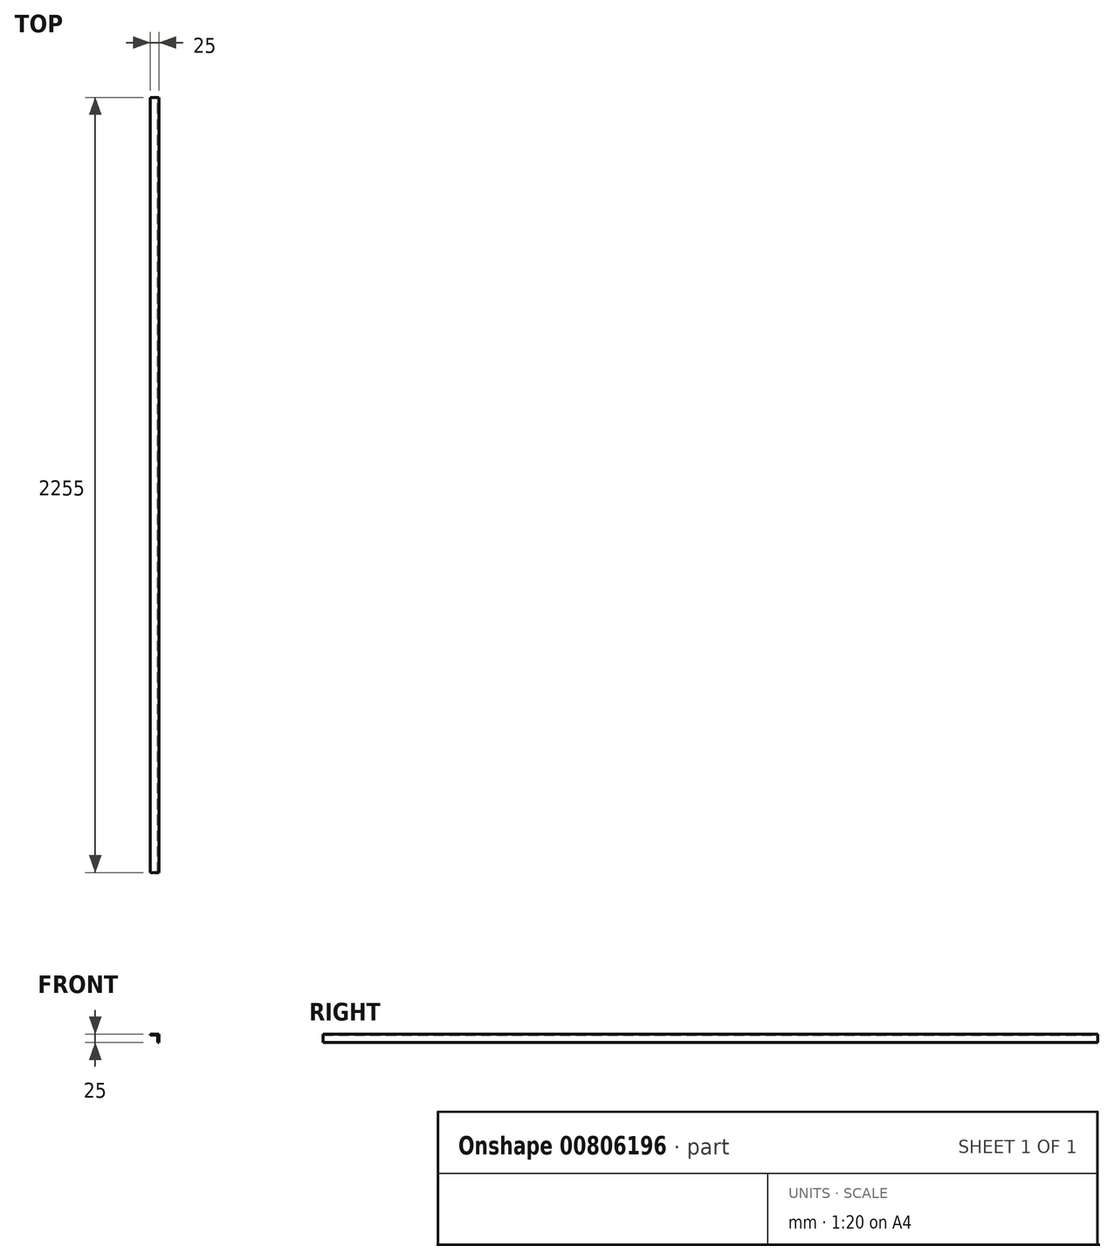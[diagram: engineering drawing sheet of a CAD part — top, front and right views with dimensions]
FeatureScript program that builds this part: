
annotation { "Feature Type Name" : "Feature", "Feature Type Description" : "" }
export const myFeature = defineFeature(function(context is Context, id is Id, definition is map)
    precondition{}
    {
        {
            var Q0;
            Q0=qCreatedBy(makeId("Front.planeOp"),FACE);
            var sketch = newSketch(context, id + "F0", { "sketchPlane" : qUnion([Q0])});
            skLineSegment(sketch, "E0.bottom", {"start": v(0, 0) * mm, "end": v(3, 0) * mm});
            skLineSegment(sketch, "E0.top", {"start": v(0, -25) * mm, "end": v(3, -25) * mm});
            skLineSegment(sketch, "E0.left", {"start": v(0, 0) * mm, "end": v(0, -25) * mm});
            skLineSegment(sketch, "E0.right", {"start": v(3, 0) * mm, "end": v(3, -25) * mm});
            skLineSegment(sketch, "E1", {"start": v(3, 0) * mm, "end": v(-22, 0) * mm});
            skLineSegment(sketch, "E2", {"start": v(-22, 0) * mm, "end": v(-22, -3) * mm});
            skLineSegment(sketch, "E3", {"start": v(-22, -3) * mm, "end": v(0, -3) * mm});
            skSolve(sketch);
        }
        {
            var Q0;
            Q0=qSketchRegion(id+"F0",true);
            extrude(context, id + "F1", {"entities" : qUnion([Q0]), "depth" : 2255 * mm, "offsetDistance" : 25 * mm});
        }
    });
